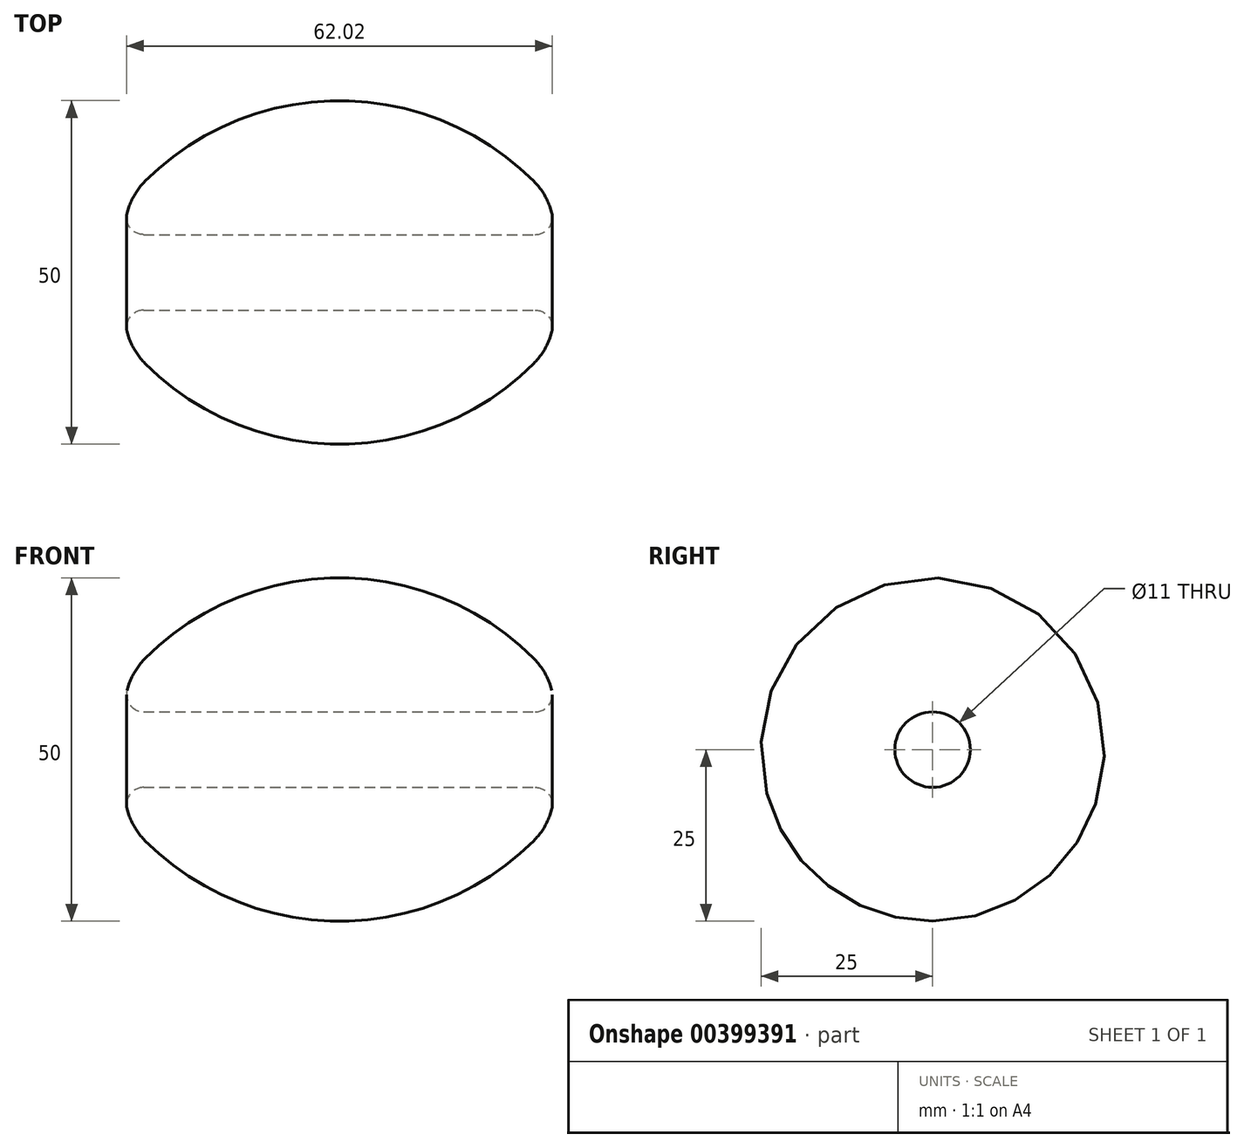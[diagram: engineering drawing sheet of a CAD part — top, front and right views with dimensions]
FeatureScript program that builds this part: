
annotation { "Feature Type Name" : "Feature", "Feature Type Description" : "" }
export const myFeature = defineFeature(function(context is Context, id is Id, definition is map)
    precondition{}
    {
        {
            var Q0;
            Q0=qCreatedBy(makeId("Front.planeOp"),FACE);
            var sketch = newSketch(context, id + "F0", { "sketchPlane" : qUnion([Q0])});
            skCircle(sketch, "E0", {"center": v(0, -15) * mm, "radius": 40 * mm});
            skLineSegment(sketch, "E1", {"start": v(-31.22, 10) * mm, "end": v(-31.22, 0) * mm});
            skLineSegment(sketch, "E2", {"start": v(-31.22, 0) * mm, "end": v(0, 0) * mm});
            skLineSegment(sketch, "E3", {"start": v(31.22, 10) * mm, "end": v(31.22, 0) * mm});
            skLineSegment(sketch, "E4", {"start": v(0, 0) * mm, "end": v(31.22, 0) * mm});
            skSolve(sketch);
        }
        {
            var Q0;
            {var subQ1=sQuery(id+"F0.wireOp",EDGE,"E1");Q0=makeQuery(id+"F0.imprint","IMPRINT",FACE,{"disambiguationData":[TD([[makeQuery(id+"F0.imprint","IMPRINT",EDGE,{"derivedFrom":subQ1}),1.0]])]});}
            var Q1;
            Q1=sQuery(id+"F0.wireOp",EDGE,"E2");
            revolve(context, id + "F1", {"entities" : qUnion([Q0]), "axis" : qUnion([Q1]), "revolveType" : RevolveType.FULL});
        }
        {
            var Q0;
            Q0=makeQuery(id+"F1.opRevolve","SWEPT_EDGE",EDGE,{"disambiguationData":[OSD([sQuery(id+"F0.wireOp",EDGE,"E0"),sQuery(id+"F0.wireOp",EDGE,"E1")])]});
            var Q1;
            Q1=makeQuery(id+"F1.opRevolve","SWEPT_EDGE",EDGE,{"disambiguationData":[OSD([sQuery(id+"F0.wireOp",EDGE,"E0"),sQuery(id+"F0.wireOp",EDGE,"E3")])]});
            fillet(context, id + "F2", {"entities" : qUnion([Q0, Q1]), "radius" : 10 * mm, "tangentPropagation" : true, "allowEdgeOverflow" : false});
        }
        {
            var Q0;
            Q0=qCreatedBy(makeId("Right.planeOp"),FACE);
            var sketch = newSketch(context, id + "F3", { "sketchPlane" : qUnion([Q0])});
            skCircle(sketch, "E5", {"center": v(0, 0) * mm, "radius": 5.5 * mm});
            skSolve(sketch);
        }
        {
            var Q0;
            Q0=makeQuery(id+"F3.imprint","IMPRINT",FACE,{"disambiguationData":[TD([[makeQuery(id+"F3.imprint","IMPRINT",EDGE,{"derivedFrom":sQuery(id+"F3.wireOp",EDGE,"E5")}),1.0]])]});
            extrude(context, id + "F4", {"entities" : qUnion([Q0]), "operationType" : NewBodyOperationType.REMOVE, "endBound" : BoundingType.SYMMETRIC, "oppositeDirection" : true, "depth" : 200 * mm});
        }
        {
            var Q0;
            Q0=makeQuery(id+"F4.boolean.opBoolean","INTERSECT",EDGE,{"derivedFrom":[makeQuery(id+"F1.opRevolve","SWEPT_FACE",FACE,{"disambiguationData":[OSD([sQuery(id+"F0.wireOp",EDGE,"E1")])]}),makeQuery(id+"F4.opExtrude","SWEPT_FACE",FACE,{"disambiguationData":[OSD([sQuery(id+"F3.wireOp",EDGE,"E5")])]})]});
            var Q1;
            Q1=makeQuery(id+"F4.boolean.opBoolean","INTERSECT",EDGE,{"derivedFrom":[makeQuery(id+"F1.opRevolve","SWEPT_FACE",FACE,{"disambiguationData":[OSD([sQuery(id+"F0.wireOp",EDGE,"E3")])]}),makeQuery(id+"F4.opExtrude","SWEPT_FACE",FACE,{"disambiguationData":[OSD([sQuery(id+"F3.wireOp",EDGE,"E5")])]})]});
            fillet(context, id + "F5", {"entities" : qUnion([Q0, Q1]), "radius" : 2.5 * mm, "tangentPropagation" : true, "allowEdgeOverflow" : false});
        }
    });
